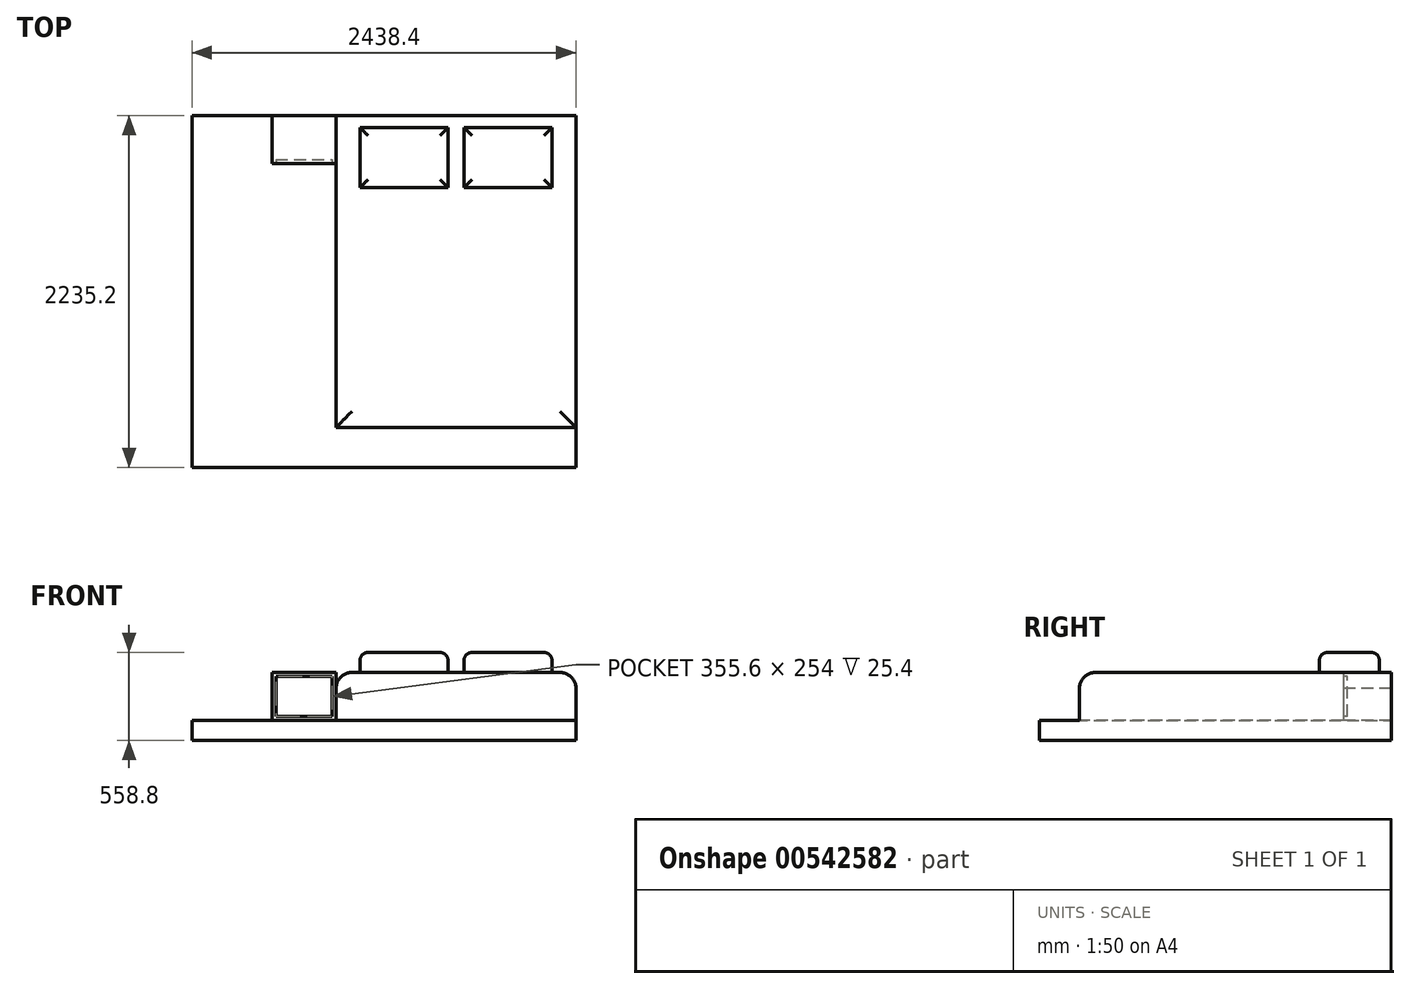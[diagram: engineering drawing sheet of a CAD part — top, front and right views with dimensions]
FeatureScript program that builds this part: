
annotation { "Feature Type Name" : "Feature", "Feature Type Description" : "" }
export const myFeature = defineFeature(function(context is Context, id is Id, definition is map)
    precondition{}
    {
        {
            var Q0;
            Q0=qCreatedBy(makeId("Top.planeOp"),FACE);
            var sketch = newSketch(context, id + "F0", { "sketchPlane" : qUnion([Q0])});
            skLineSegment(sketch, "E0.bottom", {"start": v(0, 0) * mm, "end": v(-2438.4, 0) * mm});
            skLineSegment(sketch, "E0.top", {"start": v(0, 2235.2) * mm, "end": v(-2438.4, 2235.2) * mm});
            skLineSegment(sketch, "E0.left", {"start": v(0, 0) * mm, "end": v(0, 2235.2) * mm});
            skLineSegment(sketch, "E0.right", {"start": v(-2438.4, 0) * mm, "end": v(-2438.4, 2235.2) * mm});
            skSolve(sketch);
        }
        {
            var Q0;
            Q0=makeQuery(id+"F0.imprint","IMPRINT",FACE,{"disambiguationData":[TD([[makeQuery(id+"F0.imprint","IMPRINT",EDGE,{"derivedFrom":sQuery(id+"F0.wireOp",EDGE,"E0.bottom")}),-1.0]])]});
            extrude(context, id + "F1", {"entities" : qUnion([Q0]), "depth" : 127 * mm, "offsetDistance" : 25.4 * mm});
        }
        {
            var Q0;
            Q0=makeQuery(id+"F1.opExtrude","CAP_FACE",FACE,{"disambiguationData":[OSD([sQuery(id+"F0.wireOp",EDGE,"E0.bottom"),sQuery(id+"F0.wireOp",EDGE,"E0.top"),sQuery(id+"F0.wireOp",EDGE,"E0.left"),sQuery(id+"F0.wireOp",EDGE,"E0.right")])],"isStart":false});
            var sketch = newSketch(context, id + "F2", { "sketchPlane" : qUnion([Q0])});
            skLineSegment(sketch, "E1.bottom", {"start": v(0, 2235.2) * mm, "end": v(-1524, 2235.2) * mm});
            skLineSegment(sketch, "E1.top", {"start": v(0, 254) * mm, "end": v(-1524, 254) * mm});
            skLineSegment(sketch, "E1.left", {"start": v(0, 2235.2) * mm, "end": v(0, 254) * mm});
            skLineSegment(sketch, "E1.right", {"start": v(-1524, 2235.2) * mm, "end": v(-1524, 254) * mm});
            skSolve(sketch);
        }
        {
            var Q0;
            Q0=makeQuery(id+"F2.imprint","IMPRINT",FACE,{"disambiguationData":[TD([[makeQuery(id+"F2.imprint","IMPRINT",EDGE,{"derivedFrom":sQuery(id+"F2.wireOp",EDGE,"E1.bottom")}),1.0]])]});
            extrude(context, id + "F3", {"entities" : qUnion([Q0]), "operationType" : NewBodyOperationType.ADD, "depth" : 304.8 * mm, "offsetDistance" : 25.4 * mm});
        }
        {
            var Q0;
            Q0=makeQuery(id+"F3.opExtrude","CAP_EDGE",EDGE,{"disambiguationData":[OSD([sQuery(id+"F2.wireOp",EDGE,"E1.right")])],"isStart":false});
            var Q1;
            Q1=makeQuery(id+"F3.opExtrude","CAP_EDGE",EDGE,{"disambiguationData":[OSD([sQuery(id+"F2.wireOp",EDGE,"E1.top")])],"isStart":false});
            var Q2;
            Q2=makeQuery(id+"F3.opExtrude","CAP_EDGE",EDGE,{"disambiguationData":[OSD([sQuery(id+"F2.wireOp",EDGE,"E1.left")])],"isStart":false});
            fillet(context, id + "F4", {"entities" : qUnion([Q0, Q1, Q2]), "radius" : 101.6 * mm, "tangentPropagation" : true, "allowEdgeOverflow" : false});
        }
        {
            var Q0;
            Q0=makeQuery(id+"F3.opExtrude","CAP_FACE",FACE,{"disambiguationData":[OSD([sQuery(id+"F2.wireOp",EDGE,"E1.bottom"),sQuery(id+"F2.wireOp",EDGE,"E1.top"),sQuery(id+"F2.wireOp",EDGE,"E1.left"),sQuery(id+"F2.wireOp",EDGE,"E1.right")])],"isStart":false});
            var sketch = newSketch(context, id + "F5", { "sketchPlane" : qUnion([Q0])});
            skLineSegment(sketch, "E2.bottom", {"start": v(-1371.6, 2159) * mm, "end": v(-812.8, 2159) * mm});
            skLineSegment(sketch, "E2.top", {"start": v(-1371.6, 1778) * mm, "end": v(-812.8, 1778) * mm});
            skLineSegment(sketch, "E2.left", {"start": v(-1371.6, 2159) * mm, "end": v(-1371.6, 1778) * mm});
            skLineSegment(sketch, "E2.right", {"start": v(-812.8, 2159) * mm, "end": v(-812.8, 1778) * mm});
            skLineSegment(sketch, "E3.bottom", {"start": v(-711.2, 2159) * mm, "end": v(-152.4, 2159) * mm});
            skLineSegment(sketch, "E3.top", {"start": v(-711.2, 1778) * mm, "end": v(-152.4, 1778) * mm});
            skLineSegment(sketch, "E3.left", {"start": v(-711.2, 2159) * mm, "end": v(-711.2, 1778) * mm});
            skLineSegment(sketch, "E3.right", {"start": v(-152.4, 2159) * mm, "end": v(-152.4, 1778) * mm});
            skSolve(sketch);
        }
        {
            var Q0;
            Q0=makeQuery(id+"F5.imprint","IMPRINT",FACE,{"disambiguationData":[TD([[makeQuery(id+"F5.imprint","IMPRINT",EDGE,{"derivedFrom":sQuery(id+"F5.wireOp",EDGE,"E3.bottom")}),-1.0]])]});
            var Q1;
            Q1=makeQuery(id+"F5.imprint","IMPRINT",FACE,{"disambiguationData":[TD([[makeQuery(id+"F5.imprint","IMPRINT",EDGE,{"derivedFrom":sQuery(id+"F5.wireOp",EDGE,"E2.bottom")}),-1.0]])]});
            extrude(context, id + "F6", {"entities" : qUnion([Q0, Q1]), "operationType" : NewBodyOperationType.ADD, "depth" : 127 * mm, "offsetDistance" : 25.4 * mm});
        }
        {
            var Q0;
            Q0=makeQuery(id+"F6.opExtrude","CAP_FACE",FACE,{"disambiguationData":[OSD([sQuery(id+"F5.wireOp",EDGE,"E2.bottom"),sQuery(id+"F5.wireOp",EDGE,"E2.top"),sQuery(id+"F5.wireOp",EDGE,"E2.left"),sQuery(id+"F5.wireOp",EDGE,"E2.right")])],"isStart":false});
            var Q1;
            Q1=makeQuery(id+"F6.opExtrude","CAP_FACE",FACE,{"disambiguationData":[OSD([sQuery(id+"F5.wireOp",EDGE,"E3.bottom"),sQuery(id+"F5.wireOp",EDGE,"E3.top"),sQuery(id+"F5.wireOp",EDGE,"E3.left"),sQuery(id+"F5.wireOp",EDGE,"E3.right")])],"isStart":false});
            var Q2;
            Q2=makeQuery(id+"F6.opExtrude","CAP_EDGE",EDGE,{"disambiguationData":[OSD([sQuery(id+"F5.wireOp",EDGE,"E2.top")])],"isStart":false});
            fillet(context, id + "F7", {"entities" : qUnion([Q0, Q1, Q2]), "radius" : 50.8 * mm, "tangentPropagation" : true, "allowEdgeOverflow" : false});
        }
        {
            var Q0;
            Q0=makeQuery(id+"F1.opExtrude","CAP_FACE",FACE,{"disambiguationData":[OSD([sQuery(id+"F0.wireOp",EDGE,"E0.bottom"),sQuery(id+"F0.wireOp",EDGE,"E0.top"),sQuery(id+"F0.wireOp",EDGE,"E0.left"),sQuery(id+"F0.wireOp",EDGE,"E0.right")])],"isStart":false});
            var sketch = newSketch(context, id + "F8", { "sketchPlane" : qUnion([Q0])});
            skLineSegment(sketch, "E4.bottom", {"start": v(-1524, 2235.2) * mm, "end": v(-1930.4, 2235.2) * mm});
            skLineSegment(sketch, "E4.top", {"start": v(-1524, 1930.4) * mm, "end": v(-1930.4, 1930.4) * mm});
            skLineSegment(sketch, "E4.left", {"start": v(-1524, 2235.2) * mm, "end": v(-1524, 1930.4) * mm});
            skLineSegment(sketch, "E4.right", {"start": v(-1930.4, 2235.2) * mm, "end": v(-1930.4, 1930.4) * mm});
            skSolve(sketch);
        }
        {
            var Q0;
            Q0=makeQuery(id+"F8.imprint","IMPRINT",FACE,{"disambiguationData":[TD([[makeQuery(id+"F8.imprint","IMPRINT",EDGE,{"derivedFrom":sQuery(id+"F8.wireOp",EDGE,"E4.bottom")}),1.0]])]});
            extrude(context, id + "F9", {"entities" : qUnion([Q0]), "operationType" : NewBodyOperationType.ADD, "depth" : 304.8 * mm, "offsetDistance" : 25.4 * mm});
        }
        {
            var Q0;
            Q0=makeQuery(id+"F9.opExtrude","SWEPT_FACE",FACE,{"disambiguationData":[OSD([sQuery(id+"F8.wireOp",EDGE,"E4.top")])]});
            var sketch = newSketch(context, id + "F10", { "sketchPlane" : qUnion([Q0])});
            skLineSegment(sketch, "E5.0", {"start": v(-1549.4, 152.4) * mm, "end": v(-1549.4, 355.6) * mm});
            skLineSegment(sketch, "E5.1", {"start": v(-1905, 152.4) * mm, "end": v(-1549.4, 152.4) * mm});
            skLineSegment(sketch, "E5.2", {"start": v(-1549.4, 355.6) * mm, "end": v(-1549.4, 406.4) * mm});
            skLineSegment(sketch, "E5.3", {"start": v(-1549.4, 406.4) * mm, "end": v(-1905, 406.4) * mm});
            skLineSegment(sketch, "E5.4", {"start": v(-1905, 406.4) * mm, "end": v(-1905, 152.4) * mm});
            skSolve(sketch);
        }
        {
            var Q0;
            Q0=makeQuery(id+"F10.imprint","IMPRINT",FACE,{"disambiguationData":[TD([[makeQuery(id+"F10.imprint","IMPRINT",EDGE,{"derivedFrom":sQuery(id+"F10.wireOp",EDGE,"E5.0")}),1.0]])]});
            extrude(context, id + "F11", {"entities" : qUnion([Q0]), "operationType" : NewBodyOperationType.REMOVE, "oppositeDirection" : true, "depth" : 25.4 * mm, "offsetDistance" : 25.4 * mm});
        }
    });
